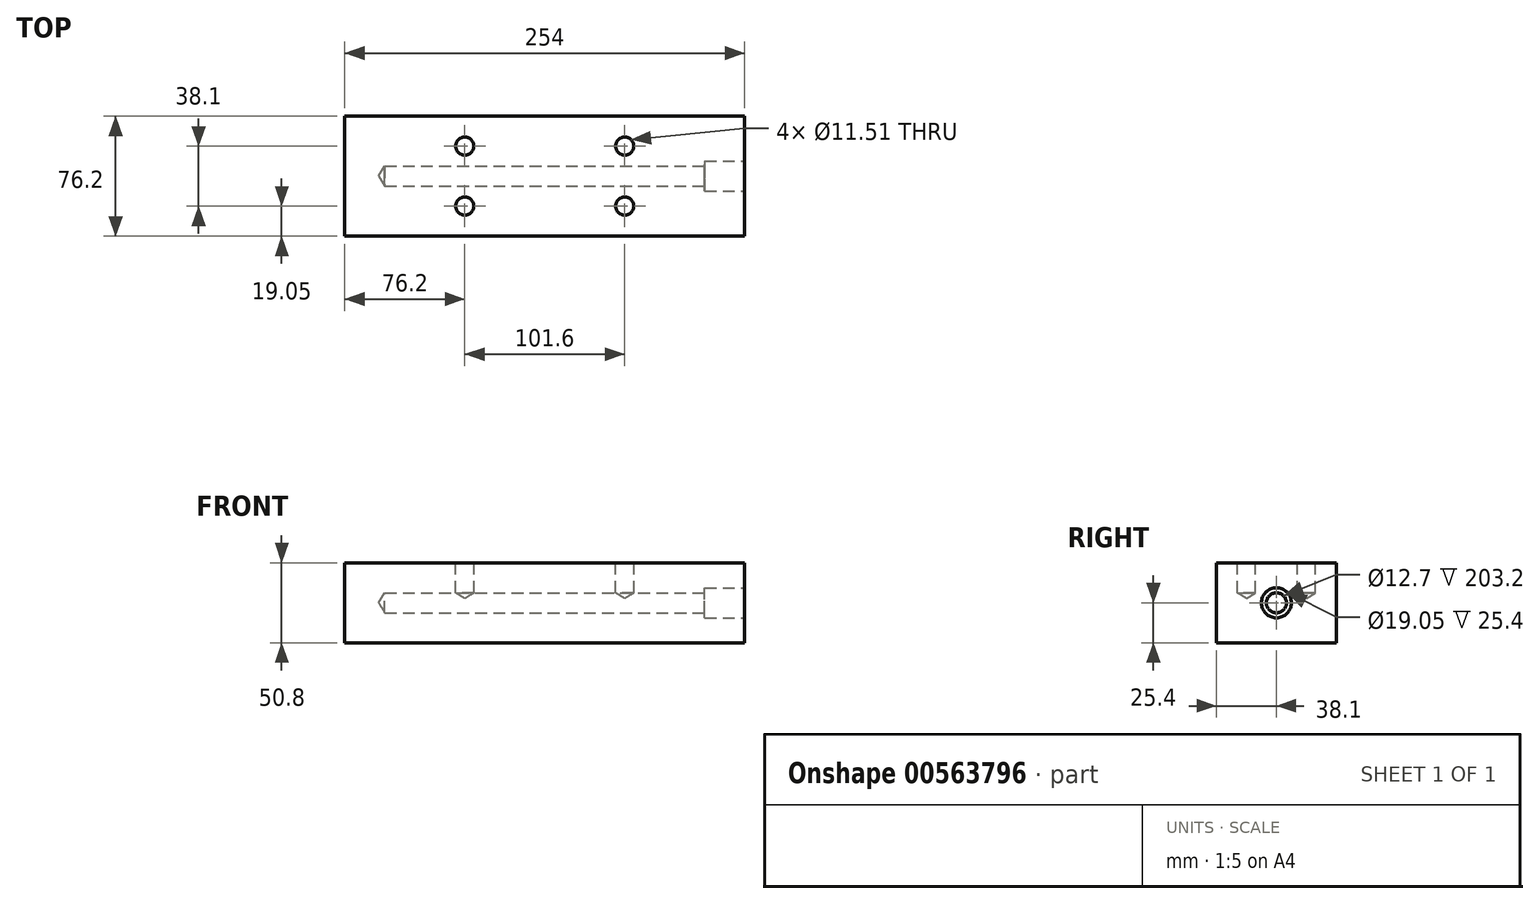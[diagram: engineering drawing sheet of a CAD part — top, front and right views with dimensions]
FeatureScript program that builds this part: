
annotation { "Feature Type Name" : "Feature", "Feature Type Description" : "" }
export const myFeature = defineFeature(function(context is Context, id is Id, definition is map)
    precondition{}
    {
        {
            var Q0;
            Q0=qCreatedBy(makeId("Top.planeOp"),FACE);
            var sketch = newSketch(context, id + "F0", { "sketchPlane" : qUnion([Q0])});
            skLineSegment(sketch, "E0.bottom", {"start": v(-127, 38.1) * mm, "end": v(127, 38.1) * mm});
            skLineSegment(sketch, "E0.top", {"start": v(-127, -38.1) * mm, "end": v(127, -38.1) * mm});
            skLineSegment(sketch, "E0.left", {"start": v(-127, 38.1) * mm, "end": v(-127, -38.1) * mm});
            skLineSegment(sketch, "E0.right", {"start": v(127, 38.1) * mm, "end": v(127, -38.1) * mm});
            skPoint(sketch, "E0.middle", {"position": v(0, 0) * mm});
            skPoint(sketch, "E1", {"position": v(-50.8, 19.05) * mm});
            skPoint(sketch, "E2.2.0.0", {"position": v(50.8, 19.05) * mm});
            skPoint(sketch, "E3.MirrorP", {"position": v(-50.8, -19.05) * mm});
            skPoint(sketch, "E4.MirrorP", {"position": v(50.8, -19.05) * mm});
            skSolve(sketch);
        }
        {
            var Q0;
            Q0=makeQuery(id+"F0.imprint","IMPRINT",FACE,{"disambiguationData":[TD([[makeQuery(id+"F0.imprint","IMPRINT",EDGE,{"derivedFrom":sQuery(id+"F0.wireOp",EDGE,"E0.bottom")}),-1.0]])]});
            extrude(context, id + "F1", {"entities" : qUnion([Q0]), "oppositeDirection" : true, "depth" : 50.8 * mm, "offsetDistance" : 25.4 * mm});
        }
        {
            var Q0;
            Q0=sQuery(id+"F0.wireOp",VERTEX,"E1");
            var Q1;
            Q1=sQuery(id+"F0.wireOp",VERTEX,"E2.2.0.0");
            var Q2;
            Q2=sQuery(id+"F0.wireOp",VERTEX,"E4.MirrorP");
            var Q3;
            Q3=sQuery(id+"F0.wireOp",VERTEX,"E3.MirrorP");
            var Q4;
            Q4=makeQuery(id+"F1.opExtrude","SWEPT_BODY",BODY,{"disambiguationData":[OSD([sQuery(id+"F0.wireOp",EDGE,"E0.bottom"),sQuery(id+"F0.wireOp",EDGE,"E0.top"),sQuery(id+"F0.wireOp",EDGE,"E0.left"),sQuery(id+"F0.wireOp",EDGE,"E0.right")])]});
            hole(context, id + "F2", {"style" : HoleStyle.SIMPLE, "endStyle" : HoleEndStyle.BLIND, "holeDiameter" : 11.5 * mm, "holeDepth" : 19.05 * mm, "isTappedThrough" : true, "tappedDepth" : 12.7 * mm, "tapClearance" : 3, "locations" : qUnion([Q0, Q1, Q2, Q3]), "scope" : qUnion([Q4])});
        }
        {
            var Q0;
            Q0=makeQuery(id+"F1.opExtrude","SWEPT_FACE",FACE,{"disambiguationData":[OSD([sQuery(id+"F0.wireOp",EDGE,"E0.right")])]});
            var sketch = newSketch(context, id + "F3", { "sketchPlane" : qUnion([Q0])});
            skPoint(sketch, "E5", {"position": v(0, -25.4) * mm});
            skSolve(sketch);
        }
        {
            var Q0;
            Q0=sQuery(id+"F3.wireOp",VERTEX,"E5");
            var Q1;
            Q1=makeQuery(id+"F1.opExtrude","SWEPT_BODY",BODY,{"disambiguationData":[OSD([sQuery(id+"F0.wireOp",EDGE,"E0.bottom"),sQuery(id+"F0.wireOp",EDGE,"E0.top"),sQuery(id+"F0.wireOp",EDGE,"E0.left"),sQuery(id+"F0.wireOp",EDGE,"E0.right")])]});
            hole(context, id + "F4", {"style" : HoleStyle.C_BORE, "endStyle" : HoleEndStyle.BLIND, "holeDiameter" : 12.7 * mm, "cBoreDiameter" : 19.05 * mm, "cBoreDepth" : 25.4 * mm, "holeDepth" : 228.6 * mm, "isTappedThrough" : true, "tappedDepth" : 12.7 * mm, "tapClearance" : 3, "locations" : qUnion([Q0]), "scope" : qUnion([Q1])});
        }
    });
